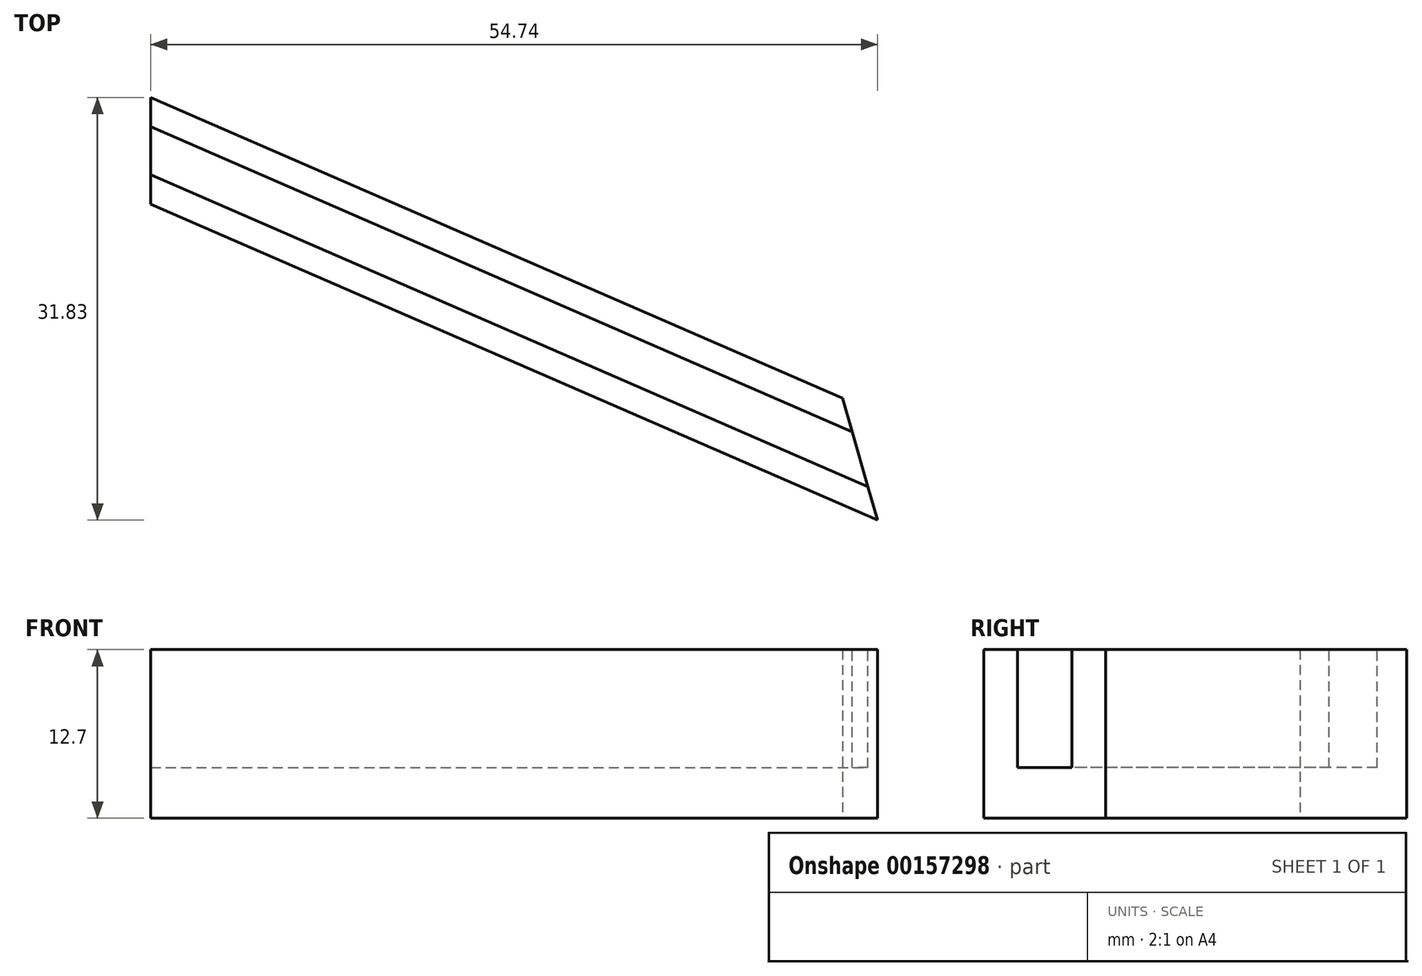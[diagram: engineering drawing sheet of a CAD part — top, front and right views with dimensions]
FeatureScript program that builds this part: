
annotation { "Feature Type Name" : "Feature", "Feature Type Description" : "" }
export const myFeature = defineFeature(function(context is Context, id is Id, definition is map)
    precondition{}
    {
        {
            var Q0;
            Q0=qCreatedBy(makeId("Top.planeOp"),FACE);
            var sketch = newSketch(context, id + "F0", { "sketchPlane" : qUnion([Q0])});
            skLineSegment(sketch, "E0", {"start": v(-7.71, 11.72) * mm, "end": v(-59.82, 34.37) * mm});
            skLineSegment(sketch, "E1", {"start": v(-59.82, 26.34) * mm, "end": v(-5.08, 2.54) * mm});
            skLineSegment(sketch, "E2", {"start": v(-5.08, 2.54) * mm, "end": v(-7.71, 11.72) * mm});
            skLineSegment(sketch, "E3", {"start": v(-59.82, 34.37) * mm, "end": v(-59.82, 26.34) * mm});
            skSolve(sketch);
        }
        {
            var Q0;
            Q0 = qSketchRegion(id + "F0", true);
            extrude(context, id + "F1", {"entities" : qUnion([Q0]), "depth" : 12.7 * mm});
        }
        {
            var Q0;
            Q0=makeQuery(id+"F1.opExtrude","CAP_FACE",FACE,{"disambiguationData":[OSD([sQuery(id+"F0.wireOp",EDGE,"E0"),sQuery(id+"F0.wireOp",EDGE,"oiM00f4o-sfL7-kbEU-8cZy-UleNWMoei6Fi"),sQuery(id+"F0.wireOp",EDGE,"QZqpGsQg-TRWu-2U9R-ufWa-PSNvCgIc1iJZ"),sQuery(id+"F0.wireOp",EDGE,"W29CwVIb-9Dfg-r9e0-Vuv3-4I0KgtQsqHT8"),sQuery(id+"F0.wireOp",EDGE,"Dkt5NUeY-tdF6-KCbD-sV6s-8N3nCH7QeNrW"),sQuery(id+"F0.wireOp",EDGE,"dy8tYV7k-2a9h-u6ov-PPCv-NYFqgSYOi5IB"),sQuery(id+"F0.wireOp",EDGE,"Fco0YpcD-LgWB-1h5o-eyFU-V6BGXKGDiEwr"),sQuery(id+"F0.wireOp",EDGE,"mAQngodi-EYc4-0Uzl-VlR3-SiMu5NFMoLtX"),sQuery(id+"F0.wireOp",EDGE,"E1"),sQuery(id+"F0.wireOp",EDGE,"E2"),sQuery(id+"F0.wireOp",EDGE,"a2dd0e33-9fa0-4f7a-8118-3b646cbb3f5f.filletArc"),sQuery(id+"F0.wireOp",EDGE,"a023f184-a8b7-4321-a8ce-4ff7c1002ffb.filletArc")])],"isStart":false});
            var sketch = newSketch(context, id + "F2", { "sketchPlane" : qUnion([Q0])});
            skLineSegment(sketch, "E4", {"start": v(-59.82, 32.16) * mm, "end": v(-6.99, 9.18) * mm});
            skLineSegment(sketch, "E5", {"start": v(-59.82, 28.56) * mm, "end": v(-5.8, 5.07) * mm});
            skLineSegment(sketch, "E6", {"start": v(-5.8, 5.07) * mm, "end": v(-6.99, 9.18) * mm});
            skLineSegment(sketch, "E7", {"start": v(-59.82, 32.16) * mm, "end": v(-59.82, 28.56) * mm});
            skSolve(sketch);
        }
        {
            var Q0;
            Q0 = qSketchRegion(id + "F2", true);
            extrude(context, id + "F3", {"entities" : qUnion([Q0]), "operationType" : NewBodyOperationType.REMOVE, "oppositeDirection" : true, "depth" : 8.9 * mm});
        }
    });
